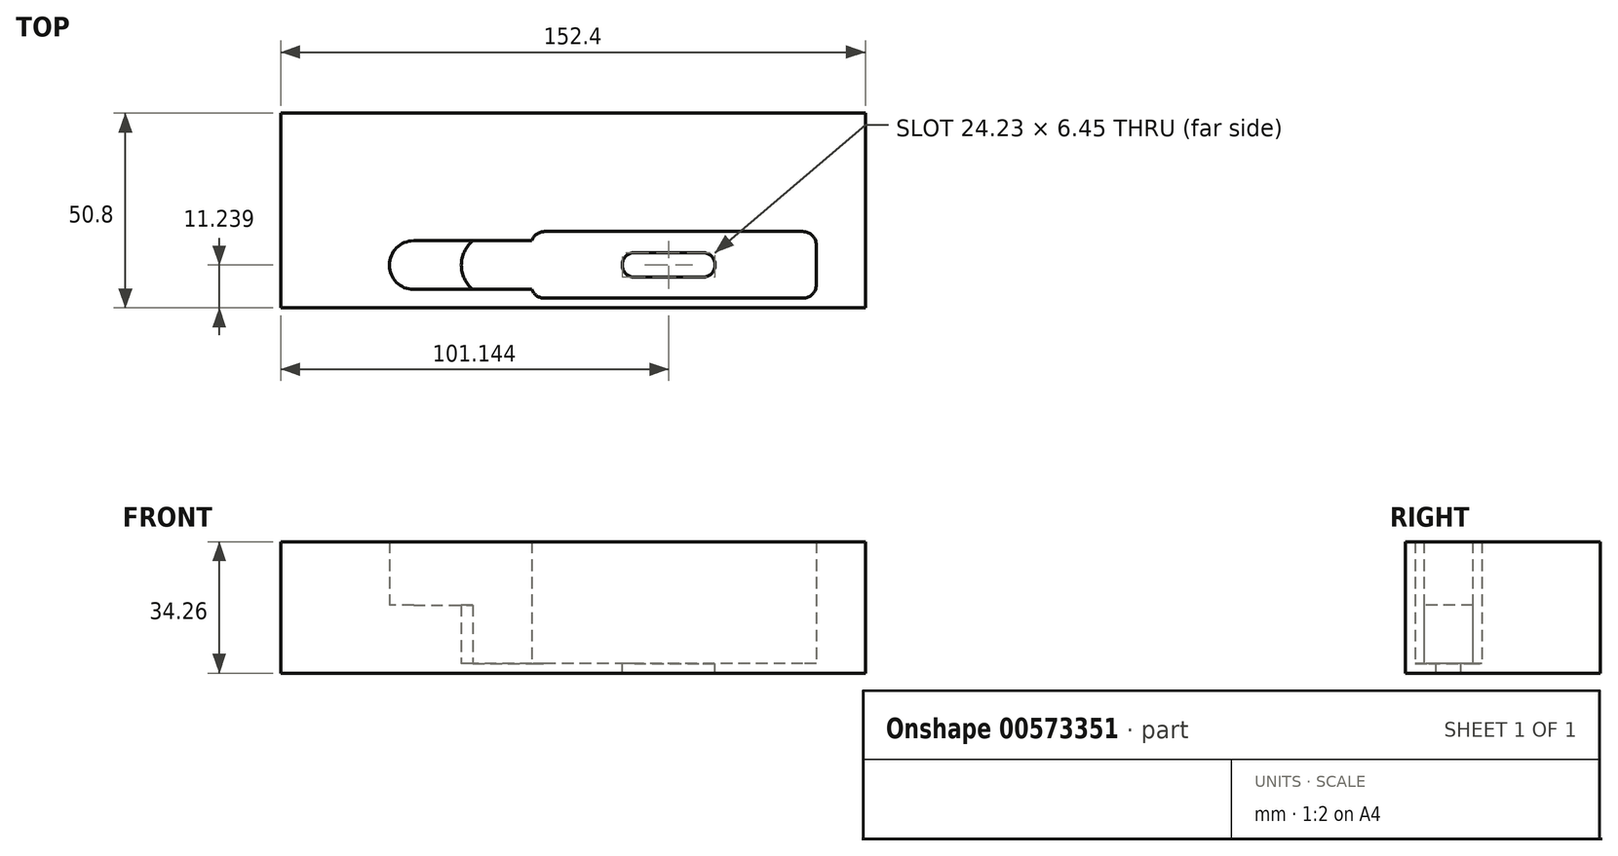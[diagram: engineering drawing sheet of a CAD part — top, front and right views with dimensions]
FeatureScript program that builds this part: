
annotation { "Feature Type Name" : "Feature", "Feature Type Description" : "" }
export const myFeature = defineFeature(function(context is Context, id is Id, definition is map)
    precondition{}
    {
        {
            var Q0;
            Q0=qCreatedBy(makeId("Top.planeOp"),FACE);
            var sketch = newSketch(context, id + "F0", { "sketchPlane" : qUnion([Q0])});
            skLineSegment(sketch, "E0.bottom", {"start": v(0, 0) * mm, "end": v(152.4, 0) * mm});
            skLineSegment(sketch, "E0.top", {"start": v(0, 50.8) * mm, "end": v(152.4, 50.8) * mm});
            skLineSegment(sketch, "E0.left", {"start": v(0, 0) * mm, "end": v(0, 50.8) * mm});
            skLineSegment(sketch, "E0.right", {"start": v(152.4, 0) * mm, "end": v(152.4, 50.8) * mm});
            skLineSegment(sketch, "E1", {"start": v(139.64, 6.05) * mm, "end": v(139.64, 16.43) * mm});
            skLineSegment(sketch, "E2", {"start": v(136.13, 19.94) * mm, "end": v(68.79, 19.94) * mm});
            skLineSegment(sketch, "E3", {"start": v(65.45, 17.53) * mm, "end": v(34.69, 17.53) * mm});
            skLineSegment(sketch, "E4", {"start": v(34.69, 4.83) * mm, "end": v(65.5, 4.83) * mm});
            skLineSegment(sketch, "E5", {"start": v(68.79, 2.54) * mm, "end": v(136.13, 2.54) * mm});
            skArc(sketch, "E6", {"start": v(34.69, 17.53) * mm, "mid": v(28.34, 11.18) * mm, "end": v(34.69, 4.83) * mm});
            skArc(sketch, "E7", {"start": v(68.79, 19.94) * mm, "mid": v(66.73, 19.27) * mm, "end": v(65.45, 17.53) * mm});
            skArc(sketch, "E8", {"start": v(139.64, 16.43) * mm, "mid": v(138.61, 18.91) * mm, "end": v(136.13, 19.94) * mm});
            skArc(sketch, "E9", {"start": v(136.13, 2.54) * mm, "mid": v(138.61, 3.57) * mm, "end": v(139.64, 6.05) * mm});
            skArc(sketch, "E10", {"start": v(65.5, 4.83) * mm, "mid": v(66.79, 3.17) * mm, "end": v(68.79, 2.54) * mm});
            skLineSegment(sketch, "E11", {"start": v(92.25, 14.46) * mm, "end": v(110.04, 14.46) * mm});
            skLineSegment(sketch, "E12", {"start": v(92.25, 8.02) * mm, "end": v(110.04, 8.02) * mm});
            skArc(sketch, "E13", {"start": v(92.25, 14.46) * mm, "mid": v(89.03, 11.24) * mm, "end": v(92.25, 8.02) * mm});
            skArc(sketch, "E14", {"start": v(110.04, 8.02) * mm, "mid": v(113.26, 11.24) * mm, "end": v(110.04, 14.46) * mm});
            skLineSegment(sketch, "E15", {"start": v(110.04, 8.02) * mm, "end": v(110.04, 2.54) * mm, "construction": true});
            skLineSegment(sketch, "E16", {"start": v(110.04, 14.46) * mm, "end": v(110.04, 19.94) * mm, "construction": true});
            skArc(sketch, "E17", {"start": v(50.1, 17.53) * mm, "mid": v(47.1, 11.18) * mm, "end": v(50.1, 4.83) * mm});
            skLineSegment(sketch, "E18", {"start": v(34.69, 11.18) * mm, "end": v(34.69, 4.83) * mm, "construction": true});
            skLineSegment(sketch, "E19", {"start": v(34.69, 11.18) * mm, "end": v(34.69, 17.53) * mm, "construction": true});
            skSolve(sketch);
        }
        {
            var Q0;
            Q0=makeQuery(id+"F0.imprint","IMPRINT",FACE,{"disambiguationData":[TD([[makeQuery(id+"F0.imprint","IMPRINT",EDGE,{"derivedFrom":sQuery(id+"F0.wireOp",EDGE,"E0.bottom")}),1.0]])]});
            extrude(context, id + "F1", {"entities" : qUnion([Q0]), "depth" : 31.72 * mm, "offsetDistance" : 25.4 * mm});
        }
        {
            var Q0;
            Q0=makeQuery(id+"F0.imprint","IMPRINT",FACE,{"disambiguationData":[TD([[makeQuery(id+"F0.imprint","IMPRINT",EDGE,{"derivedFrom":sQuery(id+"F0.wireOp",EDGE,"E1")}),1.0]])]});
            var Q1;
            Q1=makeQuery(id+"F0.imprint","IMPRINT",FACE,{"disambiguationData":[TD([[makeQuery(id+"F0.imprint","IMPRINT",EDGE,{"derivedFrom":sQuery(id+"F0.wireOp",EDGE,"E0.bottom")}),1.0]])]});
            var Q2;
            Q2=makeQuery(id+"F0.imprint","IMPRINT",FACE,{"disambiguationData":[TD([[makeQuery(id+"F0.imprint","IMPRINT",EDGE,{"derivedFrom":sQuery(id+"F0.wireOp",EDGE,"HQgcYT0F-tbi8-33aO-RdKi-TKpegETKNM7a")}),-1.0]])]});
            var Q3;
            {var subQ0=sQuery(id+"F0.wireOp",EDGE,"E6");Q3=makeQuery(id+"F0.imprint","IMPRINT",FACE,{"disambiguationData":[TD([[makeQuery(id+"F0.imprint","IMPRINT",EDGE,{"derivedFrom":subQ0}),1.0]])]});}
            extrude(context, id + "F2", {"entities" : qUnion([Q0, Q1, Q2, Q3]), "operationType" : NewBodyOperationType.ADD, "oppositeDirection" : true, "depth" : 2.54 * mm, "offsetDistance" : 25.4 * mm});
        }
        {
            var Q0;
            Q0=makeQuery(id+"F0.imprint","IMPRINT",FACE,{"disambiguationData":[TD([[makeQuery(id+"F0.imprint","IMPRINT",EDGE,{"derivedFrom":sQuery(id+"F0.wireOp",EDGE,"HQgcYT0F-tbi8-33aO-RdKi-TKpegETKNM7a")}),-1.0]])]});
            var Q1;
            {var subQ0=sQuery(id+"F0.wireOp",EDGE,"E6");Q1=makeQuery(id+"F0.imprint","IMPRINT",FACE,{"disambiguationData":[TD([[makeQuery(id+"F0.imprint","IMPRINT",EDGE,{"derivedFrom":subQ0}),1.0]])]});}
            extrude(context, id + "F3", {"entities" : qUnion([Q0, Q1]), "operationType" : NewBodyOperationType.ADD, "depth" : 15.24 * mm, "offsetDistance" : 25.4 * mm});
        }
    });
